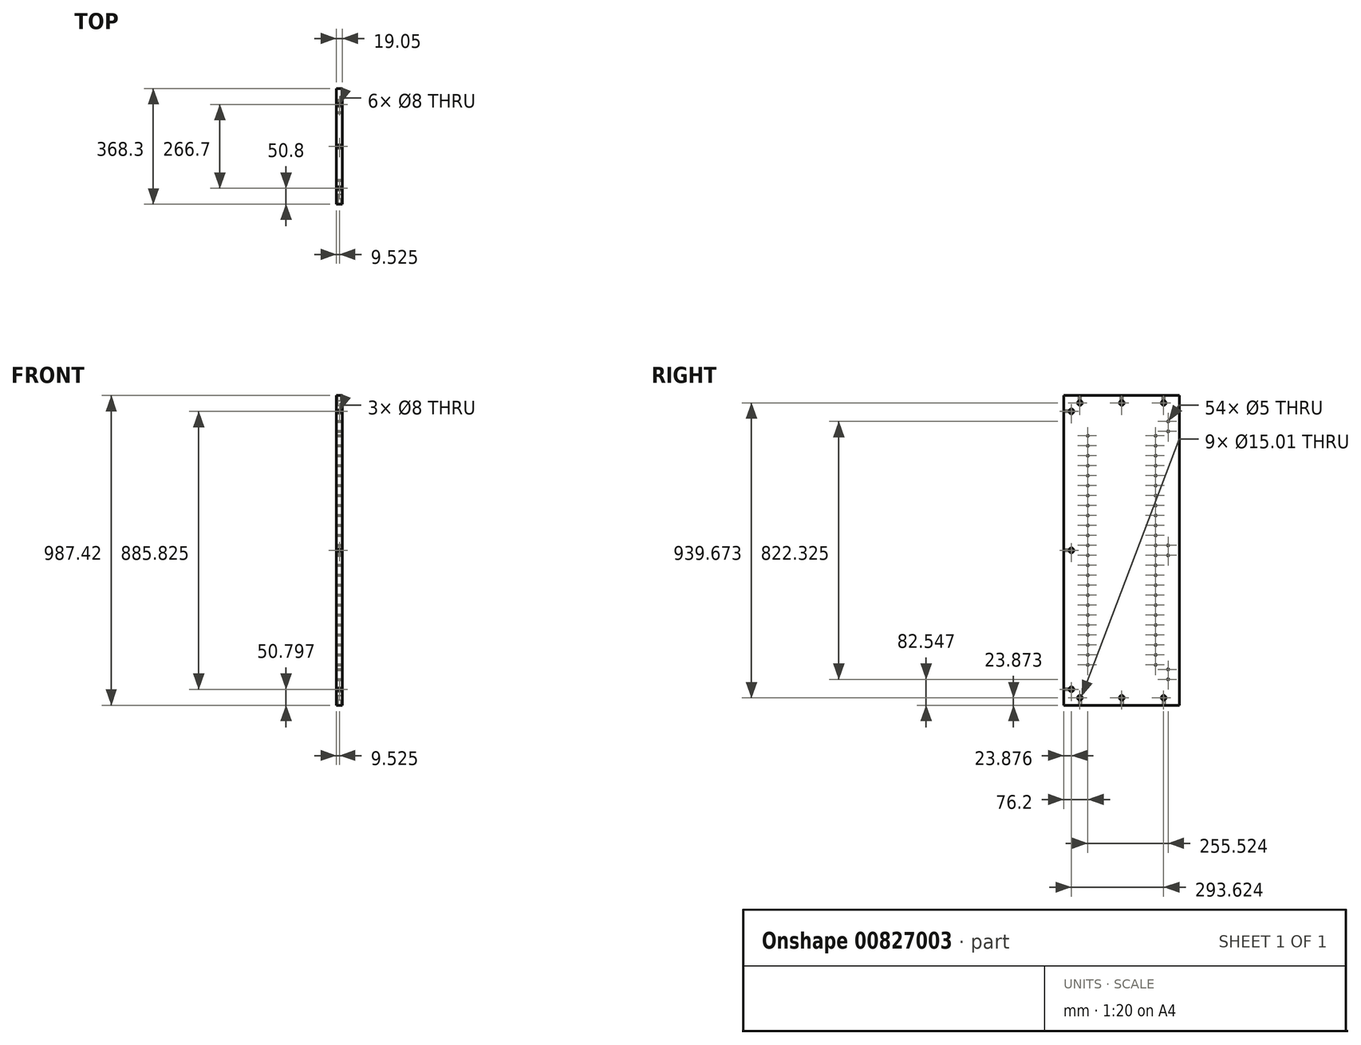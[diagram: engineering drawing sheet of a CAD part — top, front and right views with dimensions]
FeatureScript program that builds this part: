
annotation { "Feature Type Name" : "Feature", "Feature Type Description" : "" }
export const myFeature = defineFeature(function(context is Context, id is Id, definition is map)
    precondition{}
    {
        {
            var Q0;
            Q0=qCreatedBy(makeId("Right.planeOp"),FACE);
            var sketch = newSketch(context, id + "F0", { "sketchPlane" : qUnion([Q0])});
            skLineSegment(sketch, "E0.bottom", {"start": v(184.15, 493.71) * mm, "end": v(-184.15, 493.71) * mm});
            skLineSegment(sketch, "E0.top", {"start": v(184.15, -493.71) * mm, "end": v(-184.15, -493.71) * mm});
            skLineSegment(sketch, "E0.left", {"start": v(184.15, 493.71) * mm, "end": v(184.15, -493.71) * mm});
            skLineSegment(sketch, "E0.right", {"start": v(-184.15, 493.71) * mm, "end": v(-184.15, -493.71) * mm});
            skPoint(sketch, "E0.middle", {"position": v(0, 0) * mm});
            skSolve(sketch);
        }
        {
            var Q0;
            Q0=makeQuery(id+"F0.imprint","IMPRINT",FACE,{"disambiguationData":[TD([[makeQuery(id+"F0.imprint","IMPRINT",EDGE,{"derivedFrom":sQuery(id+"F0.wireOp",EDGE,"E0.bottom")}),1.0]])]});
            extrude(context, id + "F1", {"entities" : qUnion([Q0]), "depth" : 19.05 * mm, "offsetDistance" : 25.4 * mm});
        }
        {
            var Q0;
            Q0=makeQuery(id+"F1.opExtrude","CAP_FACE",FACE,{"disambiguationData":[OSD([sQuery(id+"F0.wireOp",EDGE,"E0.bottom"),sQuery(id+"F0.wireOp",EDGE,"E0.top"),sQuery(id+"F0.wireOp",EDGE,"E0.left"),sQuery(id+"F0.wireOp",EDGE,"E0.right")])],"isStart":false});
            var sketch = newSketch(context, id + "F2", { "sketchPlane" : qUnion([Q0])});
            skLineSegment(sketch, "E1", {"start": v(-184.15, 493.71) * mm, "end": v(-107.95, 493.71) * mm});
            skLineSegment(sketch, "E2", {"start": v(-107.95, 493.71) * mm, "end": v(-107.95, 365.19) * mm});
            skLineSegment(sketch, "E3.bottom", {"start": v(-107.95, 365.19) * mm, "end": v(107.95, 365.19) * mm});
            skLineSegment(sketch, "E3.top", {"start": v(-107.95, 301.69) * mm, "end": v(107.95, 301.69) * mm});
            skLineSegment(sketch, "E3.left", {"start": v(-107.95, 365.19) * mm, "end": v(-107.95, 301.69) * mm});
            skLineSegment(sketch, "E3.right", {"start": v(107.95, 365.19) * mm, "end": v(107.95, 301.69) * mm});
            skLineSegment(sketch, "E4", {"start": v(-107.95, 301.69) * mm, "end": v(-107.95, 269.94) * mm});
            skLineSegment(sketch, "E5.bottom", {"start": v(-107.95, 269.94) * mm, "end": v(107.95, 269.94) * mm});
            skLineSegment(sketch, "E5.top", {"start": v(-107.95, 206.44) * mm, "end": v(107.95, 206.44) * mm});
            skLineSegment(sketch, "E5.left", {"start": v(-107.95, 269.94) * mm, "end": v(-107.95, 206.44) * mm});
            skLineSegment(sketch, "E5.right", {"start": v(107.95, 269.94) * mm, "end": v(107.95, 206.44) * mm});
            skLineSegment(sketch, "E6", {"start": v(-107.95, 206.44) * mm, "end": v(-107.95, 174.69) * mm});
            skLineSegment(sketch, "E7.bottom", {"start": v(-107.95, 174.69) * mm, "end": v(107.95, 174.69) * mm});
            skLineSegment(sketch, "E7.top", {"start": v(-107.95, 111.19) * mm, "end": v(107.95, 111.19) * mm});
            skLineSegment(sketch, "E7.left", {"start": v(-107.95, 174.69) * mm, "end": v(-107.95, 111.19) * mm});
            skLineSegment(sketch, "E7.right", {"start": v(107.95, 174.69) * mm, "end": v(107.95, 111.19) * mm});
            skLineSegment(sketch, "E8", {"start": v(-107.95, 111.19) * mm, "end": v(-107.95, 79.44) * mm});
            skLineSegment(sketch, "E9.bottom", {"start": v(-107.95, 79.44) * mm, "end": v(107.95, 79.44) * mm});
            skLineSegment(sketch, "E9.top", {"start": v(-107.95, 15.94) * mm, "end": v(107.95, 15.94) * mm});
            skLineSegment(sketch, "E9.left", {"start": v(-107.95, 79.44) * mm, "end": v(-107.95, 15.94) * mm});
            skLineSegment(sketch, "E9.right", {"start": v(107.95, 79.44) * mm, "end": v(107.95, 15.94) * mm});
            skLineSegment(sketch, "E10", {"start": v(-107.95, 15.94) * mm, "end": v(-107.95, -15.81) * mm});
            skLineSegment(sketch, "E11.bottom", {"start": v(-107.95, -15.81) * mm, "end": v(107.95, -15.81) * mm});
            skLineSegment(sketch, "E11.top", {"start": v(-107.95, -79.31) * mm, "end": v(107.95, -79.31) * mm});
            skLineSegment(sketch, "E11.left", {"start": v(-107.95, -15.81) * mm, "end": v(-107.95, -79.31) * mm});
            skLineSegment(sketch, "E11.right", {"start": v(107.95, -15.81) * mm, "end": v(107.95, -79.31) * mm});
            skLineSegment(sketch, "E12", {"start": v(-107.95, -79.31) * mm, "end": v(-107.95, -111.06) * mm});
            skLineSegment(sketch, "E13.bottom", {"start": v(-107.95, -111.06) * mm, "end": v(107.95, -111.06) * mm});
            skLineSegment(sketch, "E13.top", {"start": v(-107.95, -174.56) * mm, "end": v(107.95, -174.56) * mm});
            skLineSegment(sketch, "E13.left", {"start": v(-107.95, -111.06) * mm, "end": v(-107.95, -174.56) * mm});
            skLineSegment(sketch, "E13.right", {"start": v(107.95, -111.06) * mm, "end": v(107.95, -174.56) * mm});
            skLineSegment(sketch, "E14", {"start": v(-107.95, -174.56) * mm, "end": v(-107.95, -206.31) * mm});
            skLineSegment(sketch, "E15.bottom", {"start": v(-107.95, -206.31) * mm, "end": v(107.95, -206.31) * mm});
            skLineSegment(sketch, "E15.top", {"start": v(-107.95, -269.81) * mm, "end": v(107.95, -269.81) * mm});
            skLineSegment(sketch, "E15.left", {"start": v(-107.95, -206.31) * mm, "end": v(-107.95, -269.81) * mm});
            skLineSegment(sketch, "E15.right", {"start": v(107.95, -206.31) * mm, "end": v(107.95, -269.81) * mm});
            skLineSegment(sketch, "E16", {"start": v(-107.95, -269.81) * mm, "end": v(-107.95, -301.56) * mm});
            skLineSegment(sketch, "E17.bottom", {"start": v(-107.95, -301.56) * mm, "end": v(107.95, -301.56) * mm});
            skLineSegment(sketch, "E17.top", {"start": v(-107.95, -365.06) * mm, "end": v(107.95, -365.06) * mm});
            skLineSegment(sketch, "E17.left", {"start": v(-107.95, -301.56) * mm, "end": v(-107.95, -365.06) * mm});
            skLineSegment(sketch, "E17.right", {"start": v(107.95, -301.56) * mm, "end": v(107.95, -365.06) * mm});
            skLineSegment(sketch, "E18", {"start": v(-184.15, 493.71) * mm, "end": v(-184.15, 411.16) * mm});
            skLineSegment(sketch, "E19", {"start": v(-184.15, 411.16) * mm, "end": v(-147.57, 411.16) * mm});
            skLineSegment(sketch, "E20", {"start": v(-147.57, 411.16) * mm, "end": v(-147.57, 379.41) * mm});
            skLineSegment(sketch, "E21", {"start": v(-184.15, -493.71) * mm, "end": v(-184.15, -411.16) * mm});
            skLineSegment(sketch, "E22", {"start": v(-184.15, -411.16) * mm, "end": v(-147.57, -411.16) * mm});
            skLineSegment(sketch, "E23", {"start": v(-147.57, -411.16) * mm, "end": v(-147.57, -379.41) * mm});
            skLineSegment(sketch, "E24", {"start": v(-184.15, 0) * mm, "end": v(-147.57, 0) * mm});
            skLineSegment(sketch, "E25", {"start": v(-147.57, 0) * mm, "end": v(-147.57, -15.88) * mm});
            skLineSegment(sketch, "E26", {"start": v(-147.57, 0) * mm, "end": v(-147.57, 15.88) * mm});
            skPoint(sketch, "E27", {"position": v(-147.57, 411.16) * mm});
            skPoint(sketch, "E28", {"position": v(-147.57, 379.41) * mm});
            skPoint(sketch, "E29", {"position": v(-147.57, 15.88) * mm});
            skPoint(sketch, "E30", {"position": v(-147.57, -15.88) * mm});
            skPoint(sketch, "E31", {"position": v(-147.57, -379.41) * mm});
            skPoint(sketch, "E32", {"position": v(-147.57, -411.16) * mm});
            skPoint(sketch, "E33", {"position": v(-107.95, 365.19) * mm});
            skPoint(sketch, "E34", {"position": v(-107.95, 333.44) * mm});
            skPoint(sketch, "E35", {"position": v(-107.95, 301.69) * mm});
            skPoint(sketch, "E36", {"position": v(-107.95, 269.94) * mm});
            skPoint(sketch, "E37", {"position": v(-107.95, 238.19) * mm});
            skPoint(sketch, "E38", {"position": v(-107.95, 206.44) * mm});
            skPoint(sketch, "E39", {"position": v(-107.95, 174.69) * mm});
            skPoint(sketch, "E40", {"position": v(-107.95, 142.94) * mm});
            skPoint(sketch, "E41", {"position": v(-107.95, 79.44) * mm});
            skPoint(sketch, "E42", {"position": v(-107.95, 47.69) * mm});
            skPoint(sketch, "E43", {"position": v(-107.95, 15.94) * mm});
            skPoint(sketch, "E44", {"position": v(-107.95, -15.81) * mm});
            skPoint(sketch, "E45", {"position": v(-107.95, -47.56) * mm});
            skPoint(sketch, "E46", {"position": v(-107.95, -79.31) * mm});
            skPoint(sketch, "E47", {"position": v(-107.95, -111.06) * mm});
            skPoint(sketch, "E48", {"position": v(-107.95, -142.81) * mm});
            skPoint(sketch, "E49", {"position": v(-107.95, -174.56) * mm});
            skPoint(sketch, "E50", {"position": v(-107.95, -206.31) * mm});
            skPoint(sketch, "E51", {"position": v(-107.95, -238.06) * mm});
            skPoint(sketch, "E52", {"position": v(-107.95, -269.81) * mm});
            skPoint(sketch, "E53", {"position": v(-107.95, -301.56) * mm});
            skPoint(sketch, "E54", {"position": v(-107.95, -333.31) * mm});
            skPoint(sketch, "E55", {"position": v(-107.95, -365.06) * mm});
            skPoint(sketch, "E56", {"position": v(107.95, -365.06) * mm});
            skPoint(sketch, "E57", {"position": v(107.95, -333.31) * mm});
            skPoint(sketch, "E58", {"position": v(107.95, -301.56) * mm});
            skPoint(sketch, "E59", {"position": v(107.95, -269.81) * mm});
            skPoint(sketch, "E60", {"position": v(107.95, -238.06) * mm});
            skPoint(sketch, "E61", {"position": v(107.95, -206.31) * mm});
            skPoint(sketch, "E62", {"position": v(107.95, -174.56) * mm});
            skPoint(sketch, "E63", {"position": v(107.95, -142.81) * mm});
            skPoint(sketch, "E64", {"position": v(107.95, -111.06) * mm});
            skPoint(sketch, "E65", {"position": v(107.95, -79.31) * mm});
            skPoint(sketch, "E66", {"position": v(107.95, -47.56) * mm});
            skPoint(sketch, "E67", {"position": v(107.95, -15.81) * mm});
            skPoint(sketch, "E68", {"position": v(107.95, 15.94) * mm});
            skPoint(sketch, "E69", {"position": v(107.95, 47.69) * mm});
            skPoint(sketch, "E70", {"position": v(107.95, 79.44) * mm});
            skPoint(sketch, "E71", {"position": v(107.95, 111.19) * mm});
            skPoint(sketch, "E72", {"position": v(107.95, 142.94) * mm});
            skPoint(sketch, "E73", {"position": v(107.95, 174.69) * mm});
            skPoint(sketch, "E74", {"position": v(107.95, 238.19) * mm});
            skPoint(sketch, "E75", {"position": v(107.95, 206.44) * mm});
            skPoint(sketch, "E76", {"position": v(107.95, 269.94) * mm});
            skPoint(sketch, "E77", {"position": v(107.95, 301.69) * mm});
            skPoint(sketch, "E78", {"position": v(107.95, 333.44) * mm});
            skPoint(sketch, "E79", {"position": v(107.95, 365.19) * mm});
            skSolve(sketch);
        }
        {
            var Q0;
            Q0=sQuery(id+"F2.wireOp",VERTEX,"E33");
            var Q1;
            Q1=sQuery(id+"F2.wireOp",VERTEX,"E35");
            var Q2;
            Q2=sQuery(id+"F2.wireOp",VERTEX,"E36");
            var Q3;
            Q3=sQuery(id+"F2.wireOp",VERTEX,"E38");
            var Q4;
            Q4=sQuery(id+"F2.wireOp",VERTEX,"E39");
            var Q5;
            Q5=sQuery(id+"F2.wireOp",VERTEX,"E7.top.start");
            var Q6;
            Q6=sQuery(id+"F2.wireOp",VERTEX,"E41");
            var Q7;
            Q7=sQuery(id+"F2.wireOp",VERTEX,"E43");
            var Q8;
            Q8=sQuery(id+"F2.wireOp",VERTEX,"E44");
            var Q9;
            Q9=sQuery(id+"F2.wireOp",VERTEX,"E45");
            var Q10;
            Q10=sQuery(id+"F2.wireOp",VERTEX,"E46");
            var Q11;
            Q11=sQuery(id+"F2.wireOp",VERTEX,"E47");
            var Q12;
            Q12=sQuery(id+"F2.wireOp",VERTEX,"E49");
            var Q13;
            Q13=sQuery(id+"F2.wireOp",VERTEX,"E50");
            var Q14;
            Q14=sQuery(id+"F2.wireOp",VERTEX,"E52");
            var Q15;
            Q15=sQuery(id+"F2.wireOp",VERTEX,"E53");
            var Q16;
            Q16=sQuery(id+"F2.wireOp",VERTEX,"E54");
            var Q17;
            Q17=sQuery(id+"F2.wireOp",VERTEX,"E55");
            var Q18;
            Q18=sQuery(id+"F2.wireOp",VERTEX,"E56");
            var Q19;
            Q19=sQuery(id+"F2.wireOp",VERTEX,"E58");
            var Q20;
            Q20=sQuery(id+"F2.wireOp",VERTEX,"E59");
            var Q21;
            Q21=sQuery(id+"F2.wireOp",VERTEX,"E61");
            var Q22;
            Q22=sQuery(id+"F2.wireOp",VERTEX,"E62");
            var Q23;
            Q23=sQuery(id+"F2.wireOp",VERTEX,"E64");
            var Q24;
            Q24=sQuery(id+"F2.wireOp",VERTEX,"E65");
            var Q25;
            Q25=sQuery(id+"F2.wireOp",VERTEX,"E67");
            var Q26;
            Q26=sQuery(id+"F2.wireOp",VERTEX,"E68");
            var Q27;
            Q27=sQuery(id+"F2.wireOp",VERTEX,"E70");
            var Q28;
            Q28=sQuery(id+"F2.wireOp",VERTEX,"E71");
            var Q29;
            Q29=sQuery(id+"F2.wireOp",VERTEX,"E73");
            var Q30;
            Q30=sQuery(id+"F2.wireOp",VERTEX,"E75");
            var Q31;
            Q31=sQuery(id+"F2.wireOp",VERTEX,"E74");
            var Q32;
            Q32=sQuery(id+"F2.wireOp",VERTEX,"E76");
            var Q33;
            Q33=sQuery(id+"F2.wireOp",VERTEX,"E77");
            var Q34;
            Q34=sQuery(id+"F2.wireOp",VERTEX,"E79");
            var Q35;
            Q35=sQuery(id+"F2.wireOp",VERTEX,"E34");
            var Q36;
            Q36=sQuery(id+"F2.wireOp",VERTEX,"E78");
            var Q37;
            Q37=sQuery(id+"F2.wireOp",VERTEX,"E37");
            var Q38;
            Q38=sQuery(id+"F2.wireOp",VERTEX,"E40");
            var Q39;
            Q39=sQuery(id+"F2.wireOp",VERTEX,"E72");
            var Q40;
            Q40=sQuery(id+"F2.wireOp",VERTEX,"E69");
            var Q41;
            Q41=sQuery(id+"F2.wireOp",VERTEX,"E42");
            var Q42;
            Q42=sQuery(id+"F2.wireOp",VERTEX,"E66");
            var Q43;
            Q43=sQuery(id+"F2.wireOp",VERTEX,"E63");
            var Q44;
            Q44=sQuery(id+"F2.wireOp",VERTEX,"E48");
            var Q45;
            Q45=sQuery(id+"F2.wireOp",VERTEX,"E51");
            var Q46;
            Q46=sQuery(id+"F2.wireOp",VERTEX,"E60");
            var Q47;
            Q47=sQuery(id+"F2.wireOp",VERTEX,"E57");
            var Q48;
            Q48=makeQuery(id+"F1.opExtrude","SWEPT_BODY",BODY,{"disambiguationData":[OSD([sQuery(id+"F0.wireOp",EDGE,"E0.bottom"),sQuery(id+"F0.wireOp",EDGE,"E0.top"),sQuery(id+"F0.wireOp",EDGE,"E0.left"),sQuery(id+"F0.wireOp",EDGE,"E0.right")])]});
            hole(context, id + "F3", {"style" : HoleStyle.SIMPLE, "endStyle" : HoleEndStyle.BLIND, "holeDiameter" : 5 * mm, "majorDiameter" : 6.35 * mm, "holeDepth" : 25.4 * mm, "isTappedThrough" : true, "tappedDepth" : 12.7 * mm, "tapClearance" : 3, "startFromSketch" : true, "locations" : qUnion([Q0, Q1, Q2, Q3, Q4, Q5, Q6, Q7, Q8, Q9, Q10, Q11, Q12, Q13, Q14, Q15, Q16, Q17, Q18, Q19, Q20, Q21, Q22, Q23, Q24, Q25, Q26, Q27, Q28, Q29, Q30, Q31, Q32, Q33, Q34, Q35, Q36, Q37, Q38, Q39, Q40, Q41, Q42, Q43, Q44, Q45, Q46, Q47]), "scope" : qUnion([Q48])});
        }
        {
            var Q0;
            Q0=makeQuery(id+"F1.opExtrude","CAP_FACE",FACE,{"disambiguationData":[OSD([sQuery(id+"F0.wireOp",EDGE,"E0.bottom"),sQuery(id+"F0.wireOp",EDGE,"E0.top"),sQuery(id+"F0.wireOp",EDGE,"E0.left"),sQuery(id+"F0.wireOp",EDGE,"E0.right")])],"isStart":false});
            var sketch = newSketch(context, id + "F4", { "sketchPlane" : qUnion([Q0])});
            skLineSegment(sketch, "E80", {"start": v(-184.15, 493.71) * mm, "end": v(-133.35, 493.71) * mm});
            skLineSegment(sketch, "E81", {"start": v(-133.35, 493.71) * mm, "end": v(-133.35, 469.84) * mm});
            skLineSegment(sketch, "E82", {"start": v(184.15, 493.71) * mm, "end": v(133.35, 493.71) * mm});
            skLineSegment(sketch, "E83", {"start": v(133.35, 493.71) * mm, "end": v(133.35, 469.84) * mm});
            skLineSegment(sketch, "E84", {"start": v(0, 493.71) * mm, "end": v(0, 469.84) * mm});
            skPoint(sketch, "E85", {"position": v(133.35, 469.84) * mm});
            skPoint(sketch, "E86", {"position": v(0, 469.84) * mm});
            skPoint(sketch, "E87", {"position": v(-133.35, 469.84) * mm});
            skLineSegment(sketch, "E88", {"start": v(-184.15, -493.71) * mm, "end": v(-133.35, -493.71) * mm});
            skLineSegment(sketch, "E89", {"start": v(-133.35, -493.71) * mm, "end": v(-133.35, -469.84) * mm});
            skLineSegment(sketch, "E90", {"start": v(184.15, -493.71) * mm, "end": v(133.35, -493.71) * mm});
            skLineSegment(sketch, "E91", {"start": v(133.35, -493.71) * mm, "end": v(133.35, -469.84) * mm});
            skLineSegment(sketch, "E92", {"start": v(0, -493.71) * mm, "end": v(0, -469.84) * mm});
            skPoint(sketch, "E93", {"position": v(-133.35, -469.84) * mm});
            skPoint(sketch, "E94", {"position": v(0, -469.84) * mm});
            skPoint(sketch, "E95", {"position": v(133.35, -469.84) * mm});
            skSolve(sketch);
        }
        {
            var Q0;
            Q0=sQuery(id+"F4.wireOp",VERTEX,"E93");
            var Q1;
            Q1=sQuery(id+"F4.wireOp",VERTEX,"E94");
            var Q2;
            Q2=sQuery(id+"F4.wireOp",VERTEX,"E95");
            var Q3;
            Q3=sQuery(id+"F4.wireOp",VERTEX,"E87");
            var Q4;
            Q4=sQuery(id+"F4.wireOp",VERTEX,"E86");
            var Q5;
            Q5=sQuery(id+"F4.wireOp",VERTEX,"E85");
            var Q6;
            Q6=makeQuery(id+"F1.opExtrude","SWEPT_BODY",BODY,{"disambiguationData":[OSD([sQuery(id+"F0.wireOp",EDGE,"E0.bottom"),sQuery(id+"F0.wireOp",EDGE,"E0.top"),sQuery(id+"F0.wireOp",EDGE,"E0.left"),sQuery(id+"F0.wireOp",EDGE,"E0.right")])]});
            hole(context, id + "F5", {"style" : HoleStyle.SIMPLE, "endStyle" : HoleEndStyle.BLIND, "holeDiameter" : 15 * mm, "majorDiameter" : 6.35 * mm, "holeDepth" : 14.22 * mm, "isTappedThrough" : true, "tappedDepth" : 12.7 * mm, "tapClearance" : 3, "startFromSketch" : true, "locations" : qUnion([Q0, Q1, Q2, Q3, Q4, Q5]), "scope" : qUnion([Q6])});
        }
        {
            var Q0;
            Q0=sQuery(id+"F2.wireOp",VERTEX,"E27");
            var Q1;
            Q1=sQuery(id+"F2.wireOp",VERTEX,"E28");
            var Q2;
            Q2=sQuery(id+"F2.wireOp",VERTEX,"E29");
            var Q3;
            Q3=sQuery(id+"F2.wireOp",VERTEX,"E30");
            var Q4;
            Q4=sQuery(id+"F2.wireOp",VERTEX,"E31");
            var Q5;
            Q5=sQuery(id+"F2.wireOp",VERTEX,"E32");
            var Q6;
            Q6=makeQuery(id+"F1.opExtrude","SWEPT_BODY",BODY,{"disambiguationData":[OSD([sQuery(id+"F0.wireOp",EDGE,"E0.bottom"),sQuery(id+"F0.wireOp",EDGE,"E0.top"),sQuery(id+"F0.wireOp",EDGE,"E0.left"),sQuery(id+"F0.wireOp",EDGE,"E0.right")])]});
            hole(context, id + "F6", {"style" : HoleStyle.SIMPLE, "endStyle" : HoleEndStyle.BLIND, "holeDiameter" : 5 * mm, "majorDiameter" : 6.35 * mm, "holeDepth" : 14.22 * mm, "isTappedThrough" : true, "tappedDepth" : 12.7 * mm, "tapClearance" : 3, "startFromSketch" : true, "locations" : qUnion([Q0, Q1, Q2, Q3, Q4, Q5]), "scope" : qUnion([Q6])});
        }
        {
            var Q0;
            Q0=makeQuery(id+"F1.opExtrude","CAP_FACE",FACE,{"disambiguationData":[OSD([sQuery(id+"F0.wireOp",EDGE,"E0.bottom"),sQuery(id+"F0.wireOp",EDGE,"E0.top"),sQuery(id+"F0.wireOp",EDGE,"E0.left"),sQuery(id+"F0.wireOp",EDGE,"E0.right")])],"isStart":false});
            var sketch = newSketch(context, id + "F7", { "sketchPlane" : qUnion([Q0])});
            skLineSegment(sketch, "E96", {"start": v(184.15, 493.71) * mm, "end": v(160.27, 493.71) * mm});
            skLineSegment(sketch, "E97", {"start": v(160.27, 493.71) * mm, "end": v(160.27, 442.91) * mm});
            skLineSegment(sketch, "E98", {"start": v(184.15, -493.71) * mm, "end": v(160.27, -493.71) * mm});
            skLineSegment(sketch, "E99", {"start": v(160.27, -493.71) * mm, "end": v(160.27, -442.91) * mm});
            skLineSegment(sketch, "E100", {"start": v(184.15, 0) * mm, "end": v(160.27, 0) * mm});
            skSolve(sketch);
        }
        {
            var Q0;
            Q0=sQuery(id+"F7.wireOp",VERTEX,"E97.end");
            var Q1;
            Q1=sQuery(id+"F7.wireOp",VERTEX,"E100.end");
            var Q2;
            Q2=sQuery(id+"F7.wireOp",VERTEX,"E99.end");
            var Q3;
            Q3=makeQuery(id+"F1.opExtrude","SWEPT_BODY",BODY,{"disambiguationData":[OSD([sQuery(id+"F0.wireOp",EDGE,"E0.bottom"),sQuery(id+"F0.wireOp",EDGE,"E0.top"),sQuery(id+"F0.wireOp",EDGE,"E0.left"),sQuery(id+"F0.wireOp",EDGE,"E0.right")])]});
            hole(context, id + "F8", {"style" : HoleStyle.SIMPLE, "endStyle" : HoleEndStyle.BLIND, "holeDiameter" : 15 * mm, "majorDiameter" : 6.35 * mm, "holeDepth" : 14.22 * mm, "isTappedThrough" : true, "tappedDepth" : 12.7 * mm, "tapClearance" : 3, "startFromSketch" : true, "locations" : qUnion([Q0, Q1, Q2]), "scope" : qUnion([Q3])});
        }
        {
            var Q0;
            Q0=makeQuery(id+"F1.opExtrude","SWEPT_FACE",FACE,{"disambiguationData":[OSD([sQuery(id+"F0.wireOp",EDGE,"E0.top")])]});
            var sketch = newSketch(context, id + "F9", { "sketchPlane" : qUnion([Q0])});
            skLineSegment(sketch, "E101", {"start": v(9.53, 184.15) * mm, "end": v(9.53, 133.35) * mm});
            skLineSegment(sketch, "E102", {"start": v(9.53, -184.15) * mm, "end": v(9.53, -133.35) * mm});
            skLineSegment(sketch, "E103", {"start": v(0, 0) * mm, "end": v(9.53, 0) * mm});
            skPoint(sketch, "E104", {"position": v(9.53, 133.35) * mm});
            skPoint(sketch, "E105", {"position": v(9.53, 0) * mm});
            skPoint(sketch, "E106", {"position": v(9.53, -133.35) * mm});
            skSolve(sketch);
        }
        {
            var Q0;
            Q0=sQuery(id+"F9.wireOp",VERTEX,"E104");
            var Q1;
            Q1=sQuery(id+"F9.wireOp",VERTEX,"E105");
            var Q2;
            Q2=sQuery(id+"F9.wireOp",VERTEX,"E106");
            var Q3;
            Q3=makeQuery(id+"F1.opExtrude","SWEPT_BODY",BODY,{"disambiguationData":[OSD([sQuery(id+"F0.wireOp",EDGE,"E0.bottom"),sQuery(id+"F0.wireOp",EDGE,"E0.top"),sQuery(id+"F0.wireOp",EDGE,"E0.left"),sQuery(id+"F0.wireOp",EDGE,"E0.right")])]});
            hole(context, id + "F10", {"style" : HoleStyle.SIMPLE, "endStyle" : HoleEndStyle.BLIND, "holeDiameter" : 8 * mm, "majorDiameter" : 6.35 * mm, "holeDepth" : 25.4 * mm, "isTappedThrough" : true, "tappedDepth" : 12.7 * mm, "tapClearance" : 3, "startFromSketch" : true, "locations" : qUnion([Q0, Q1, Q2]), "scope" : qUnion([Q3])});
        }
        {
            var Q0;
            Q0=makeQuery(id+"F1.opExtrude","SWEPT_FACE",FACE,{"disambiguationData":[OSD([sQuery(id+"F0.wireOp",EDGE,"E0.bottom")])]});
            var sketch = newSketch(context, id + "F11", { "sketchPlane" : qUnion([Q0])});
            skLineSegment(sketch, "E107", {"start": v(9.53, 184.15) * mm, "end": v(9.53, 133.35) * mm});
            skLineSegment(sketch, "E108", {"start": v(9.53, -184.15) * mm, "end": v(9.53, -133.35) * mm});
            skLineSegment(sketch, "E109", {"start": v(0, 0) * mm, "end": v(9.53, 0) * mm});
            skPoint(sketch, "E110", {"position": v(9.53, 133.35) * mm});
            skPoint(sketch, "E111", {"position": v(9.53, 0) * mm});
            skPoint(sketch, "E112", {"position": v(9.53, -133.35) * mm});
            skSolve(sketch);
        }
        {
            var Q0;
            Q0=sQuery(id+"F11.wireOp",VERTEX,"E110");
            var Q1;
            Q1=sQuery(id+"F11.wireOp",VERTEX,"E111");
            var Q2;
            Q2=sQuery(id+"F11.wireOp",VERTEX,"E112");
            var Q3;
            Q3=makeQuery(id+"F1.opExtrude","SWEPT_BODY",BODY,{"disambiguationData":[OSD([sQuery(id+"F0.wireOp",EDGE,"E0.bottom"),sQuery(id+"F0.wireOp",EDGE,"E0.top"),sQuery(id+"F0.wireOp",EDGE,"E0.left"),sQuery(id+"F0.wireOp",EDGE,"E0.right")])]});
            hole(context, id + "F12", {"style" : HoleStyle.SIMPLE, "endStyle" : HoleEndStyle.BLIND, "holeDiameter" : 8 * mm, "majorDiameter" : 6.35 * mm, "holeDepth" : 25.4 * mm, "isTappedThrough" : true, "tappedDepth" : 12.7 * mm, "tapClearance" : 3, "startFromSketch" : true, "locations" : qUnion([Q0, Q1, Q2]), "scope" : qUnion([Q3])});
        }
        {
            var Q0;
            Q0=makeQuery(id+"F1.opExtrude","SWEPT_FACE",FACE,{"disambiguationData":[OSD([sQuery(id+"F0.wireOp",EDGE,"E0.left")])]});
            var sketch = newSketch(context, id + "F13", { "sketchPlane" : qUnion([Q0])});
            skLineSegment(sketch, "E113", {"start": v(-9.53, 493.71) * mm, "end": v(-9.53, 442.91) * mm});
            skLineSegment(sketch, "E114", {"start": v(-9.53, -493.71) * mm, "end": v(-9.53, -442.91) * mm});
            skLineSegment(sketch, "E115", {"start": v(0, 0) * mm, "end": v(-9.53, 0) * mm});
            skSolve(sketch);
        }
        {
            var Q0;
            Q0=sQuery(id+"F13.wireOp",VERTEX,"E114.end");
            var Q1;
            Q1=sQuery(id+"F13.wireOp",VERTEX,"E115.end");
            var Q2;
            Q2=sQuery(id+"F13.wireOp",VERTEX,"E113.end");
            var Q3;
            Q3=makeQuery(id+"F1.opExtrude","SWEPT_BODY",BODY,{"disambiguationData":[OSD([sQuery(id+"F0.wireOp",EDGE,"E0.bottom"),sQuery(id+"F0.wireOp",EDGE,"E0.top"),sQuery(id+"F0.wireOp",EDGE,"E0.left"),sQuery(id+"F0.wireOp",EDGE,"E0.right")])]});
            hole(context, id + "F14", {"style" : HoleStyle.SIMPLE, "endStyle" : HoleEndStyle.BLIND, "holeDiameter" : 8 * mm, "majorDiameter" : 6.35 * mm, "holeDepth" : 25.4 * mm, "isTappedThrough" : true, "tappedDepth" : 12.7 * mm, "tapClearance" : 3, "startFromSketch" : true, "locations" : qUnion([Q0, Q1, Q2]), "scope" : qUnion([Q3])});
        }
        {
            var Q0;
            Q0=makeQuery(id+"F1.opExtrude","SWEPT_BODY",BODY,{"disambiguationData":[OSD([sQuery(id+"F0.wireOp",EDGE,"E0.bottom"),sQuery(id+"F0.wireOp",EDGE,"E0.top"),sQuery(id+"F0.wireOp",EDGE,"E0.left"),sQuery(id+"F0.wireOp",EDGE,"E0.right")])]});
            var Q1;
            Q1=makeQuery(id+"F1.opExtrude","SWEPT_FACE",FACE,{"disambiguationData":[OSD([sQuery(id+"F0.wireOp",EDGE,"E0.left")])]});
            mirror(context, id + "F15", {"entities" : qUnion([Q0]), "mirrorPlane" : qUnion([Q1])});
        }
        {
            var Q0;
            Q0=makeQuery(id+"F1.opExtrude","SWEPT_BODY",BODY,{"disambiguationData":[OSD([sQuery(id+"F0.wireOp",EDGE,"E0.bottom"),sQuery(id+"F0.wireOp",EDGE,"E0.top"),sQuery(id+"F0.wireOp",EDGE,"E0.left"),sQuery(id+"F0.wireOp",EDGE,"E0.right")])]});
            deleteBodies(context, id + "F16", {"entities" : qUnion([Q0])});
        }
    });
